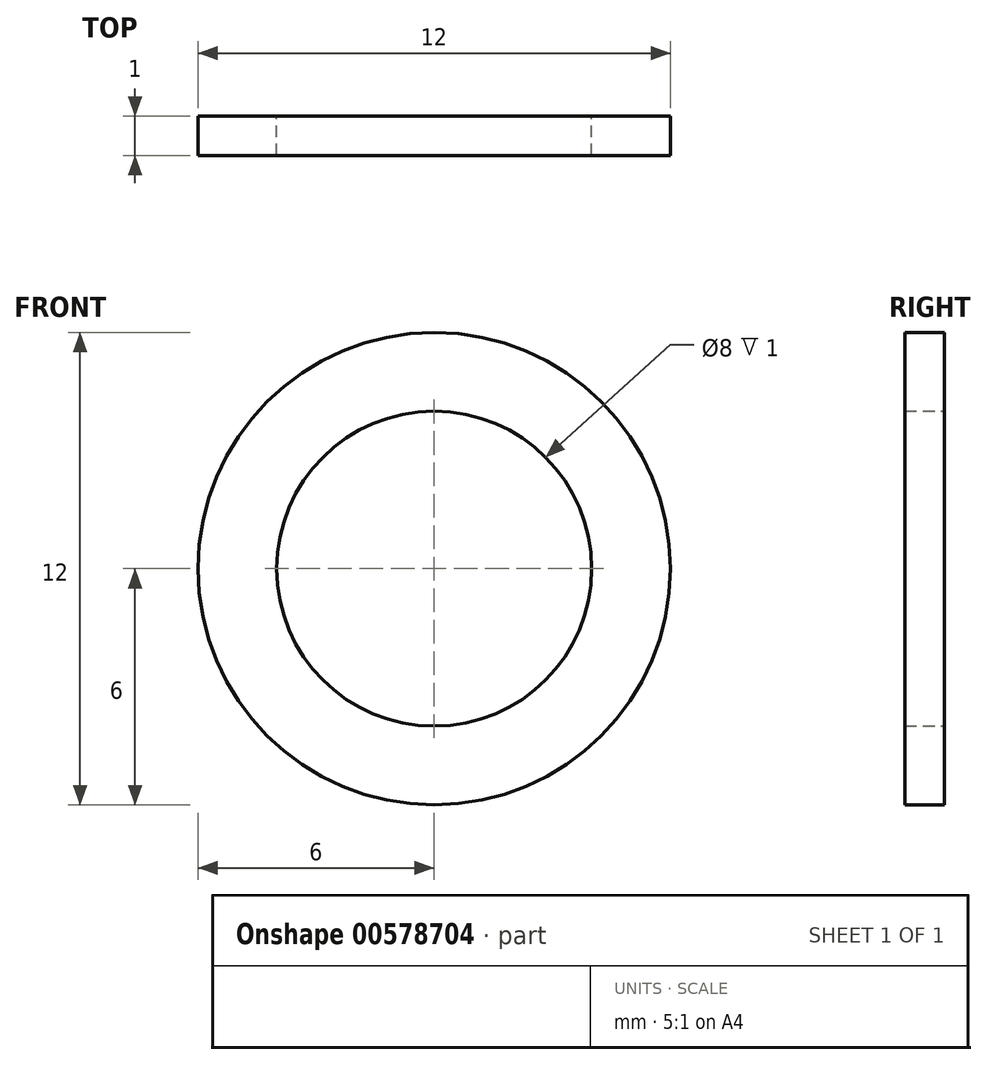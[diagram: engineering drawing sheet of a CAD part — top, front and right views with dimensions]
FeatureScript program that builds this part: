
annotation { "Feature Type Name" : "Feature", "Feature Type Description" : "" }
export const myFeature = defineFeature(function(context is Context, id is Id, definition is map)
    precondition{}
    {
        {
            var Q0;
            Q0=qCreatedBy(makeId("Front.planeOp"),FACE);
            var sketch = newSketch(context, id + "F0", { "sketchPlane" : qUnion([Q0])});
            skCircle(sketch, "E0", {"center": v(0, 0) * mm, "radius": 6 * mm});
            skCircle(sketch, "E1", {"center": v(0, 0) * mm, "radius": 4 * mm});
            skSolve(sketch);
        }
        {
            var Q0;
            Q0 = qSketchRegion(id + "F0", true);
            extrude(context, id + "F1", {"entities" : qUnion([Q0]), "depth" : 1 * mm, "offsetDistance" : 25 * mm});
        }
    });
